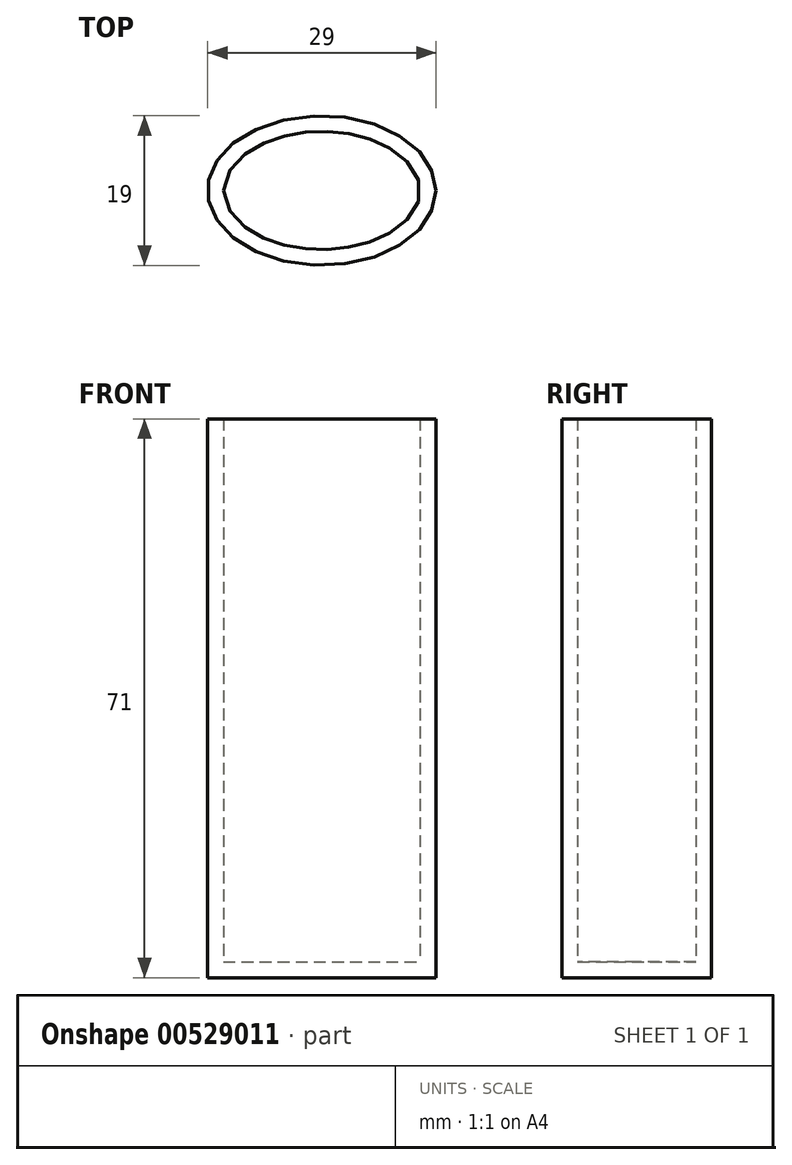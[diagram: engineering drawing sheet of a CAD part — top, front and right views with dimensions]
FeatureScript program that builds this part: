
annotation { "Feature Type Name" : "Feature", "Feature Type Description" : "" }
export const myFeature = defineFeature(function(context is Context, id is Id, definition is map)
    precondition{}
    {
        {
            var Q0;
            Q0=qCreatedBy(makeId("Top.planeOp"),FACE);
            var sketch = newSketch(context, id + "F0", { "sketchPlane" : qUnion([Q0])});
            skEllipse(sketch, "E0", {"center": v(-3.3, -8.74) * mm, "majorRadius": 14.5 * mm, "minorRadius": 9.5 * mm, "majorAxis": v(1, 0)});
            skPoint(sketch, "E1", {"position": v(-17.8, -8.74) * mm});
            skPoint(sketch, "E2", {"position": v(11.2, -8.74) * mm});
            skPoint(sketch, "E3", {"position": v(-3.3, 0.76) * mm});
            skPoint(sketch, "E4", {"position": v(-3.3, -18.24) * mm});
            skSolve(sketch);
        }
        {
            var Q0;
            Q0 = qSketchRegion(id + "F0", true);
            extrude(context, id + "F1", {"entities" : qUnion([Q0]), "depth" : 71 * mm, "offsetDistance" : 25 * mm});
        }
        {
            var Q0;
            Q0=makeQuery(id+"F1.opExtrude","CAP_FACE",FACE,{"disambiguationData":[OSD([sQuery(id+"F0.wireOp",EDGE,"E0")])],"isStart":false});
            shell(context, id + "F2", {"entities" : qUnion([Q0]), "thickness" : 2 * mm});
        }
    });
